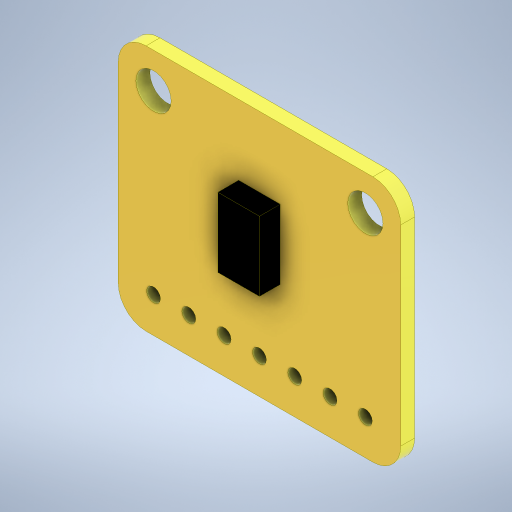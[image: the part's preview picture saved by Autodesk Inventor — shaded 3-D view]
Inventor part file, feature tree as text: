
AUTODESK INVENTOR PART (.ipt)
format: ipt  version: 2023 (Build 270158000, 158)  size: 279,552 bytes
history: native  units: mm
features: extrude x2, sketch x2
ambient origin geometry x8: Origin, YZ Plane, XZ Plane, XY Plane, X Axis, Y Axis, Z Axis, Center Point
bodies: Solid1 (feature_tree)
feature tree (4):
  extrude  "Extrusion1"  Depth=17.78mm
  extrude  "Extrusion2"  Depth=1.5mm
  sketch  "Sketch1"  dims[d0=20.32mm d1=17.78mm]
  sketch  "Sketch2"  dims[d2=15.24mm d3=2.54mm d4=2.54mm d5=2.0mm d6=1.0mm d7=0.0mm d8=2.54mm d9=1.0mm d10=40.0mm d12=2.54mm d13=40.0mm d15=2.54mm d18=3.0mm d19=5.0mm d21=7.5mm d22=1.5mm d23=0.0mm]
